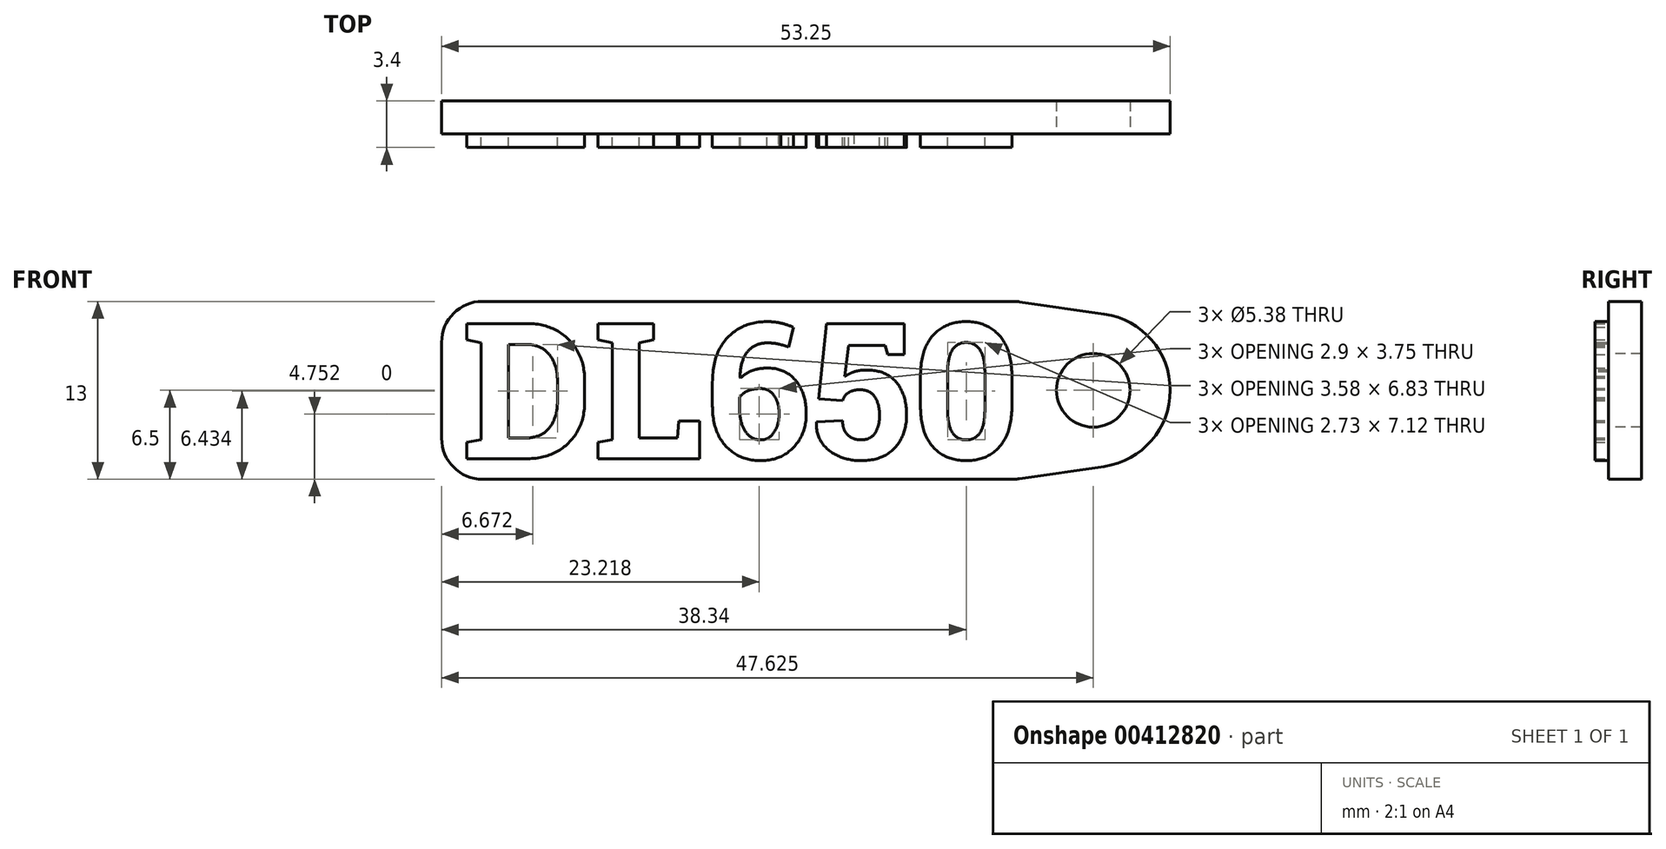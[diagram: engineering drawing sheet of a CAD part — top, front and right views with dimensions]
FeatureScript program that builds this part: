
annotation { "Feature Type Name" : "Feature", "Feature Type Description" : "" }
export const myFeature = defineFeature(function(context is Context, id is Id, definition is map)
    precondition{}
    {
        {
            var Q0;
            Q0=qCreatedBy(makeId("Front.planeOp"),FACE);
            var sketch = newSketch(context, id + "F0", { "sketchPlane" : qUnion([Q0])});
            skText(sketch, "E0", { "text": "DL650", "fontName": "RobotoSlab-Bold.ttf"});
            const initialGuessF0  = {"E0": [-0.02053, -0.01, 1, 0, 0.01]};
            skSetInitialGuess(sketch, initialGuessF0);
            skSolve(sketch);
        }
        {
            var Q0;
            Q0=qSketchRegion(id+"F0",true);
            extrude(context, id + "F1", {"entities" : qUnion([Q0]), "depth" : 1 * mm});
        }
        {
            var Q0;
            Q0=qCreatedBy(makeId("Front.planeOp"),FACE);
            var sketch = newSketch(context, id + "F2", { "sketchPlane" : qUnion([Q0])});
            skLineSegment(sketch, "E1", {"start": v(20, -11.5) * mm, "end": v(-22, -11.5) * mm});
            skLineSegment(sketch, "E2", {"start": v(-22, 1.5) * mm, "end": v(20, 1.5) * mm});
            skLineSegment(sketch, "E3", {"start": v(20, -11.5) * mm, "end": v(20, 1.5) * mm, "construction": true});
            skLineSegment(sketch, "E4", {"start": v(-22, -11.5) * mm, "end": v(-22, 1.5) * mm});
            skCircle(sketch, "E5", {"center": v(25.63, -5) * mm, "radius": 5.62 * mm});
            skLineSegment(sketch, "E6", {"start": v(20, -5) * mm, "end": v(67.35, -5) * mm, "construction": true});
            skPoint(sketch, "E6.endSnap0", {"position": v(20, -5) * mm});
            skLineSegment(sketch, "E7", {"start": v(20, 1.5) * mm, "end": v(26.43, 0.57) * mm});
            skLineSegment(sketch, "E8", {"start": v(26.43, -10.57) * mm, "end": v(20, -11.5) * mm});
            skCircle(sketch, "E9", {"center": v(25.63, -5) * mm, "radius": 2.69 * mm});
            skSolve(sketch);
        }
        {
            var Q0;
            Q0=qSketchRegion(id+"F2",true);
            extrude(context, id + "F3", {"entities" : qUnion([Q0]), "oppositeDirection" : true, "offsetDistance" : 25 * mm, "depth" : 2.4 * mm});
        }
        {
            var Q0;
            Q0=makeQuery(id+"F3.opExtrude","SWEPT_EDGE",EDGE,{"disambiguationData":[OSD([sQuery(id+"F2.wireOp",EDGE,"E2"),sQuery(id+"F2.wireOp",EDGE,"E4")])]});
            var Q1;
            Q1=makeQuery(id+"F3.opExtrude","SWEPT_EDGE",EDGE,{"disambiguationData":[OSD([sQuery(id+"F2.wireOp",EDGE,"E1"),sQuery(id+"F2.wireOp",EDGE,"E4")])]});
            var Q2;
            Q2=makeQuery(id+"F3.opExtrude","SWEPT_EDGE",EDGE,{"disambiguationData":[OSD([sQuery(id+"F2.wireOp",EDGE,"E1"),sQuery(id+"F2.wireOp",EDGE,"E8")])]});
            var Q3;
            Q3=makeQuery(id+"F3.opExtrude","SWEPT_EDGE",EDGE,{"disambiguationData":[OSD([sQuery(id+"F2.wireOp",EDGE,"E2"),sQuery(id+"F2.wireOp",EDGE,"E7")])]});
            fillet(context, id + "F4", {"entities" : qUnion([Q0, Q1, Q2, Q3]), "radius" : 3 * mm, "tangentPropagation" : true, "allowEdgeOverflow" : false});
        }
    });
